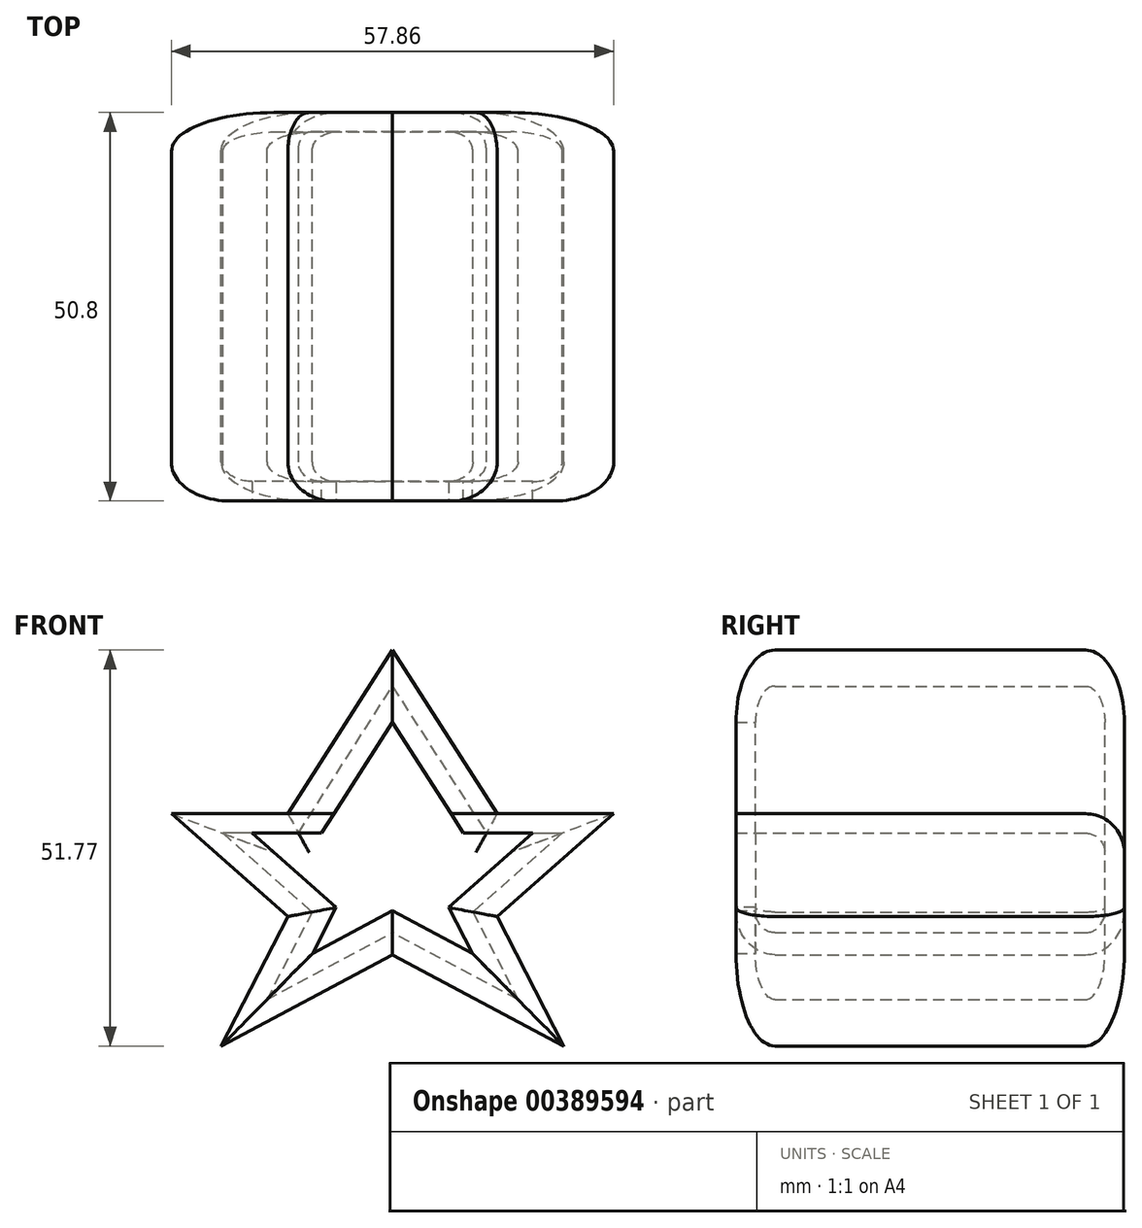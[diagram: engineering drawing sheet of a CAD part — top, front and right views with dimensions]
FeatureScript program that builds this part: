
annotation { "Feature Type Name" : "Feature", "Feature Type Description" : "" }
export const myFeature = defineFeature(function(context is Context, id is Id, definition is map)
    precondition{}
    {
        {
            var Q0;
            Q0=qCreatedBy(makeId("Front.planeOp"),FACE);
            var sketch = newSketch(context, id + "F0", { "sketchPlane" : qUnion([Q0])});
            skLineSegment(sketch, "E0", {"start": v(-13.69, 0) * mm, "end": v(0, 21.4) * mm});
            skLineSegment(sketch, "E1", {"start": v(0, 21.4) * mm, "end": v(13.69, 0) * mm});
            skLineSegment(sketch, "E2", {"start": v(-13.69, 0) * mm, "end": v(-28.93, 0) * mm});
            skLineSegment(sketch, "E3", {"start": v(13.69, 0) * mm, "end": v(28.93, 0) * mm});
            skLineSegment(sketch, "E4", {"start": v(-28.93, 0) * mm, "end": v(-13.69, -13.44) * mm});
            skLineSegment(sketch, "E5", {"start": v(28.93, 0) * mm, "end": v(13.69, -13.44) * mm});
            skLineSegment(sketch, "E6", {"start": v(-13.69, -13.44) * mm, "end": v(-22.42, -30.37) * mm});
            skLineSegment(sketch, "E7", {"start": v(-22.42, -30.37) * mm, "end": v(0, -18.43) * mm});
            skLineSegment(sketch, "E8", {"start": v(13.69, -13.44) * mm, "end": v(22.42, -30.37) * mm});
            skLineSegment(sketch, "E9", {"start": v(22.42, -30.37) * mm, "end": v(0, -18.43) * mm});
            skSolve(sketch);
        }
        {
            var Q0;
            Q0 = qSketchRegion(id + "F0", true);
            extrude(context, id + "F1", {"entities" : qUnion([Q0]), "depth" : 50.8 * mm});
        }
        {
            var Q0;
            Q0=makeQuery(id+"F1.opExtrude","CAP_EDGE",EDGE,{"disambiguationData":[OSD([sQuery(id+"F0.wireOp",EDGE,"E0")])],"isStart":false});
            var Q1;
            Q1=makeQuery(id+"F1.opExtrude","CAP_EDGE",EDGE,{"disambiguationData":[OSD([sQuery(id+"F0.wireOp",EDGE,"E1")])],"isStart":false});
            var Q2;
            Q2=makeQuery(id+"F1.opExtrude","CAP_EDGE",EDGE,{"disambiguationData":[OSD([sQuery(id+"F0.wireOp",EDGE,"E7")])],"isStart":false});
            var Q3;
            Q3=makeQuery(id+"F1.opExtrude","CAP_EDGE",EDGE,{"disambiguationData":[OSD([sQuery(id+"F0.wireOp",EDGE,"E9")])],"isStart":false});
            var Q4;
            Q4=makeQuery(id+"F1.opExtrude","CAP_EDGE",EDGE,{"disambiguationData":[OSD([sQuery(id+"F0.wireOp",EDGE,"E5")])],"isStart":false});
            var Q5;
            Q5=makeQuery(id+"F1.opExtrude","CAP_EDGE",EDGE,{"disambiguationData":[OSD([sQuery(id+"F0.wireOp",EDGE,"E4")])],"isStart":false});
            var Q6;
            Q6=makeQuery(id+"F1.opExtrude","CAP_EDGE",EDGE,{"disambiguationData":[OSD([sQuery(id+"F0.wireOp",EDGE,"E6")])],"isStart":false});
            var Q7;
            Q7=makeQuery(id+"F1.opExtrude","CAP_EDGE",EDGE,{"disambiguationData":[OSD([sQuery(id+"F0.wireOp",EDGE,"E8")])],"isStart":false});
            fillet(context, id + "F2", {"entities" : qUnion([Q0, Q1, Q2, Q3, Q4, Q5, Q6, Q7]), "radius" : 5.08 * mm, "tangentPropagation" : true, "allowEdgeOverflow" : false});
        }
        {
            var Q0;
            Q0=makeQuery(id+"F1.opExtrude","CAP_EDGE",EDGE,{"disambiguationData":[OSD([sQuery(id+"F0.wireOp",EDGE,"E3")])],"isStart":true});
            var Q1;
            Q1=makeQuery(id+"F1.opExtrude","CAP_EDGE",EDGE,{"disambiguationData":[OSD([sQuery(id+"F0.wireOp",EDGE,"E2")])],"isStart":true});
            var Q2;
            Q2=makeQuery(id+"F1.opExtrude","CAP_EDGE",EDGE,{"disambiguationData":[OSD([sQuery(id+"F0.wireOp",EDGE,"E0")])],"isStart":true});
            var Q3;
            Q3=makeQuery(id+"F1.opExtrude","CAP_EDGE",EDGE,{"disambiguationData":[OSD([sQuery(id+"F0.wireOp",EDGE,"E1")])],"isStart":true});
            var Q4;
            Q4=makeQuery(id+"F1.opExtrude","CAP_EDGE",EDGE,{"disambiguationData":[OSD([sQuery(id+"F0.wireOp",EDGE,"E9")])],"isStart":true});
            var Q5;
            Q5=makeQuery(id+"F1.opExtrude","CAP_EDGE",EDGE,{"disambiguationData":[OSD([sQuery(id+"F0.wireOp",EDGE,"E7")])],"isStart":true});
            var Q6;
            Q6=makeQuery(id+"F1.opExtrude","CAP_EDGE",EDGE,{"disambiguationData":[OSD([sQuery(id+"F0.wireOp",EDGE,"E8")])],"isStart":true});
            var Q7;
            Q7=makeQuery(id+"F1.opExtrude","CAP_EDGE",EDGE,{"disambiguationData":[OSD([sQuery(id+"F0.wireOp",EDGE,"E4")])],"isStart":true});
            var Q8;
            Q8=makeQuery(id+"F1.opExtrude","CAP_EDGE",EDGE,{"disambiguationData":[OSD([sQuery(id+"F0.wireOp",EDGE,"E6")])],"isStart":true});
            var Q9;
            Q9=makeQuery(id+"F1.opExtrude","CAP_EDGE",EDGE,{"disambiguationData":[OSD([sQuery(id+"F0.wireOp",EDGE,"E5")])],"isStart":true});
            fillet(context, id + "F3", {"entities" : qUnion([Q0, Q1, Q2, Q3, Q4, Q5, Q6, Q7, Q8, Q9]), "radius" : 5.08 * mm, "tangentPropagation" : true, "allowEdgeOverflow" : false});
        }
        {
            var Q0;
            Q0=makeQuery(id+"F1.opExtrude","CAP_FACE",FACE,{"disambiguationData":[OSD([sQuery(id+"F0.wireOp",EDGE,"E0"),sQuery(id+"F0.wireOp",EDGE,"E1"),sQuery(id+"F0.wireOp",EDGE,"E2"),sQuery(id+"F0.wireOp",EDGE,"E3"),sQuery(id+"F0.wireOp",EDGE,"E4"),sQuery(id+"F0.wireOp",EDGE,"E5"),sQuery(id+"F0.wireOp",EDGE,"E6"),sQuery(id+"F0.wireOp",EDGE,"E7"),sQuery(id+"F0.wireOp",EDGE,"E8"),sQuery(id+"F0.wireOp",EDGE,"E9")])],"isStart":false});
            shell(context, id + "F4", {"entities" : qUnion([Q0]), "thickness" : 2.54 * mm});
        }
    });
